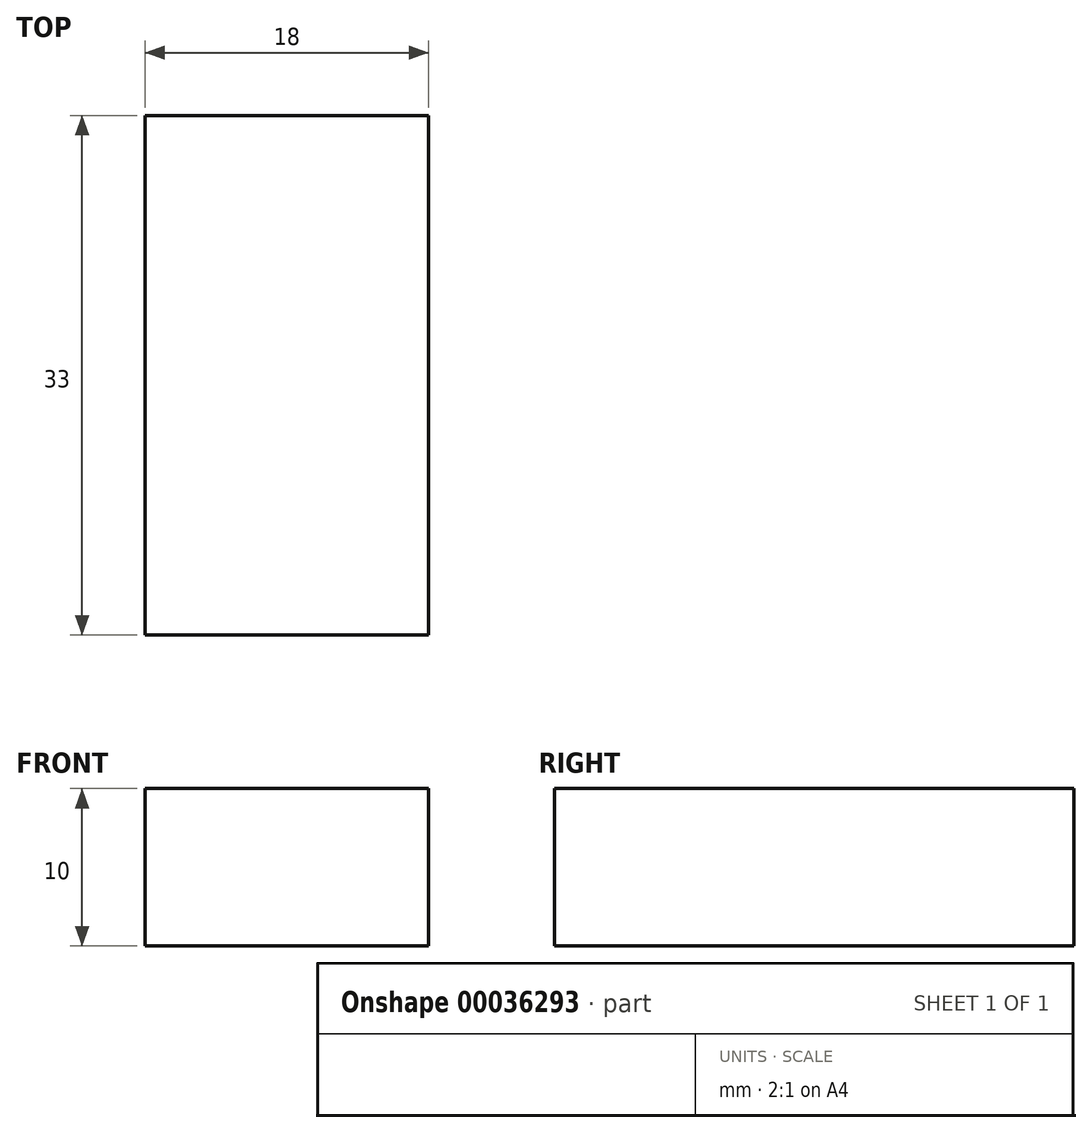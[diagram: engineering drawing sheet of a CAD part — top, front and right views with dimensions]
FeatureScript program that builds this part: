
annotation { "Feature Type Name" : "Feature", "Feature Type Description" : "" }
export const myFeature = defineFeature(function(context is Context, id is Id, definition is map)
    precondition{}
    {
        {
            var Q0;
            Q0=qCreatedBy(makeId("Top.planeOp"),FACE);
            var sketch = newSketch(context, id + "F0", { "sketchPlane" : qUnion([Q0])});
            skLineSegment(sketch, "E0.bottom", {"start": v(0, 0) * mm, "end": v(18, 0) * mm});
            skLineSegment(sketch, "E0.top", {"start": v(0, -33) * mm, "end": v(18, -33) * mm});
            skLineSegment(sketch, "E0.left", {"start": v(0, 0) * mm, "end": v(0, -33) * mm});
            skLineSegment(sketch, "E0.right", {"start": v(18, 0) * mm, "end": v(18, -33) * mm});
            skSolve(sketch);
        }
        {
            var Q0;
            Q0=makeQuery(id+"F0.imprint","IMPRINT",FACE,{"disambiguationData":[TD([[makeQuery(id+"F0.imprint","IMPRINT",EDGE,{"derivedFrom":sQuery(id+"F0.wireOp",EDGE,"E0.bottom")}),-1.0]])]});
            extrude(context, id + "F1", {"entities" : qUnion([Q0]), "depth" : 10 * mm});
        }
    });
